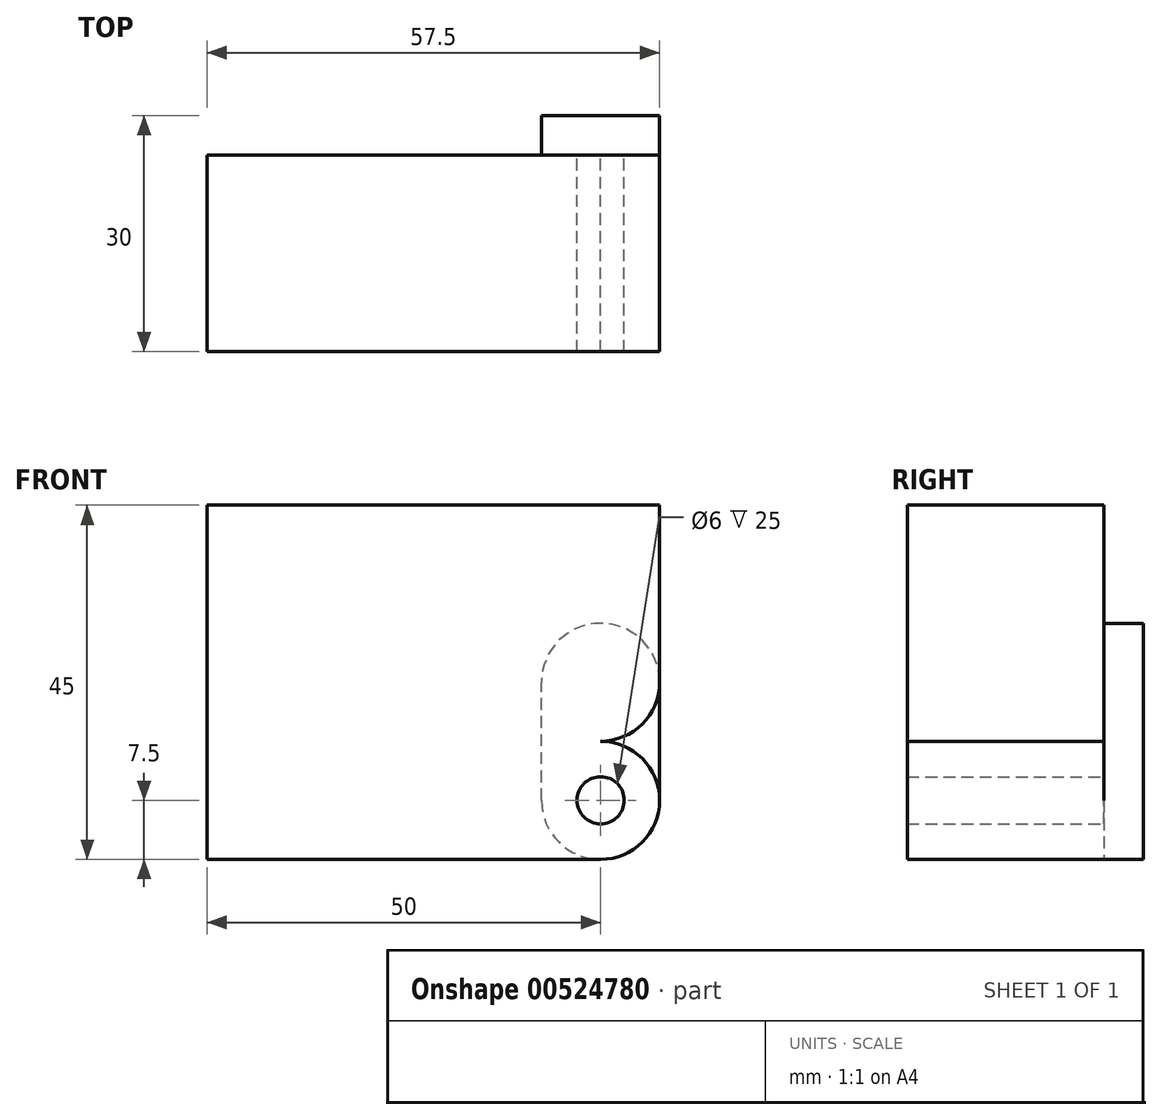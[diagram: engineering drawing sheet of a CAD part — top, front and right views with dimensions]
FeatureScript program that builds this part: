
annotation { "Feature Type Name" : "Feature", "Feature Type Description" : "" }
export const myFeature = defineFeature(function(context is Context, id is Id, definition is map)
    precondition{}
    {
        {
            var Q0;
            Q0=qCreatedBy(makeId("Front.planeOp"),FACE);
            var sketch = newSketch(context, id + "F0", { "sketchPlane" : qUnion([Q0])});
            skLineSegment(sketch, "E0.bottom", {"start": v(0, 0) * mm, "end": v(-50, 0) * mm});
            skLineSegment(sketch, "E0.top", {"start": v(0, 15) * mm, "end": v(-50, 15) * mm, "construction": true});
            skLineSegment(sketch, "E0.left", {"start": v(0, 0) * mm, "end": v(0, 15) * mm, "construction": true});
            skLineSegment(sketch, "E0.right", {"start": v(-50, 0) * mm, "end": v(-50, 15) * mm});
            skArc(sketch, "E1", {"start": v(0, 15) * mm, "mid": v(7.5, 7.5) * mm, "end": v(0, 0) * mm});
            skArc(sketch, "E2.MirrorCS", {"start": v(0, -15) * mm, "mid": v(7.5, -7.5) * mm, "end": v(0, 0) * mm});
            skLineSegment(sketch, "E3.MirrorCS", {"start": v(0, -15) * mm, "end": v(-50, -15) * mm});
            skLineSegment(sketch, "E4.MirrorCS", {"start": v(-50, 0) * mm, "end": v(-50, -15) * mm});
            skLineSegment(sketch, "E5.MirrorCS", {"start": v(0, 0) * mm, "end": v(0, -15) * mm, "construction": true});
            skCircle(sketch, "E6", {"center": v(0, 7.5) * mm, "radius": 3 * mm});
            skCircle(sketch, "E7.MirrorC", {"center": v(0, -7.5) * mm, "radius": 3 * mm});
            skLineSegment(sketch, "E8", {"start": v(7.5, 7.5) * mm, "end": v(7.5, 30) * mm});
            skLineSegment(sketch, "E9", {"start": v(7.5, 30) * mm, "end": v(-50, 30) * mm});
            skLineSegment(sketch, "E10", {"start": v(-50, 30) * mm, "end": v(-50, 15) * mm});
            skSolve(sketch);
        }
        {
            var Q0;
            Q0=makeQuery(id+"F0.imprint","IMPRINT",FACE,{"disambiguationData":[TD([[makeQuery(id+"F0.imprint","IMPRINT",EDGE,{"derivedFrom":sQuery(id+"F0.wireOp",EDGE,"E0.right")}),-1.0]])]});
            var Q1;
            Q1 = qSketchRegion(id + "FjbwSUm8XobSmaI_0", true);
            extrude(context, id + "F1", {"entities" : qUnion([Q0, Q1]), "depth" : 25 * mm, "offsetDistance" : 25 * mm});
        }
        {
            var Q0;
            Q0=makeQuery(id+"F0.imprint","IMPRINT",FACE,{"disambiguationData":[TD([[makeQuery(id+"F0.imprint","IMPRINT",EDGE,{"derivedFrom":sQuery(id+"F0.wireOp",EDGE,"E2.MirrorCS")}),1.0]])]});
            extrude(context, id + "F2", {"entities" : qUnion([Q0]), "depth" : 25 * mm, "offsetDistance" : 25 * mm});
        }
        {
            var Q0;
            Q0=makeQuery(id+"F0.imprint","IMPRINT",FACE,{"disambiguationData":[TD([[makeQuery(id+"F0.imprint","IMPRINT",EDGE,{"derivedFrom":sQuery(id+"F0.wireOp",EDGE,"E6")}),1.0]])]});
            var Q1;
            Q1=makeQuery(id+"F0.imprint","IMPRINT",FACE,{"disambiguationData":[TD([[makeQuery(id+"F0.imprint","IMPRINT",EDGE,{"derivedFrom":sQuery(id+"F0.wireOp",EDGE,"E7.MirrorC")}),-1.0]])]});
            extrude(context, id + "F3", {"entities" : qUnion([Q0, Q1]), "depth" : 25 * mm, "offsetDistance" : 25 * mm});
        }
        {
            var Q0;
            Q0=qCreatedBy(makeId("Front.planeOp"),FACE);
            var sketch = newSketch(context, id + "F4", { "sketchPlane" : qUnion([Q0])});
            skArc(sketch, "E11.0", {"start": v(0, 15) * mm, "mid": v(5.3, 12.8) * mm, "end": v(7.5, 7.5) * mm});
            skArc(sketch, "E11.1", {"start": v(0, -15) * mm, "mid": v(5.3, -12.8) * mm, "end": v(7.5, -7.5) * mm});
            skPoint(sketch, "E12.0", {"position": v(7.5, 7.5) * mm});
            skLineSegment(sketch, "E13", {"start": v(7.5, -7.5) * mm, "end": v(7.5, 7.5) * mm});
            skPoint(sketch, "E14.orphan", {"position": v(0, 0) * mm});
            skArc(sketch, "E15.MirrorCS", {"start": v(0, -15) * mm, "mid": v(-5.3, -12.8) * mm, "end": v(-7.5, -7.5) * mm});
            skLineSegment(sketch, "E16.MirrorCS", {"start": v(-7.5, -7.5) * mm, "end": v(-7.5, 7.5) * mm});
            skArc(sketch, "E17.MirrorCS", {"start": v(0, 15) * mm, "mid": v(-5.3, 12.8) * mm, "end": v(-7.5, 7.5) * mm});
            skSolve(sketch);
        }
        {
            var Q0;
            Q0 = qSketchRegion(id + "F4", true);
            extrude(context, id + "F5", {"entities" : qUnion([Q0]), "operationType" : NewBodyOperationType.ADD, "oppositeDirection" : true, "depth" : 5 * mm, "offsetDistance" : 25 * mm});
        }
    });
